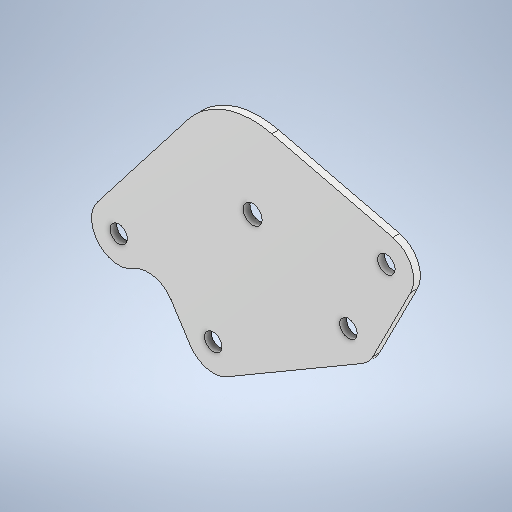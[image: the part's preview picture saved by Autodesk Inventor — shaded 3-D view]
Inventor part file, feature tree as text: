
AUTODESK INVENTOR PART (.ipt)
format: ipt  version: 2025.2 (Build 292293000, 293)  size: 270,336 bytes
history: native  units: in
note: dims shown in document units (in); Inventor stores cm internally (conversion verified against a paired STEP export)
features: other x5, sketch x2, plane x1, sheet_metal_op x1, extrude x1, reference x1
ambient origin geometry x8: Origin, YZ Plane, XZ Plane, XY Plane, X Axis, Y Axis, Z Axis, Center Point
bodies: Body1 (feature_tree)
feature tree (11):
  plane  "Work Plane1"
  sheet_metal_op  "Face3"
  extrude  "Extrusion1"  Depth=0.16in
  sketch  "Sketch1"  dims[d1=0.5in d14=0.16in]
  reference  "Reference3"
  other  "Plate3"
  sketch  "Sketch2"  dims[d15=0.0625in d16=0.175in d17=0.175in d18=0.625in d19=0.0in]
  parser-record x1  (decoder bookkeeping rows leaked as tree rows — omitted from the tree; the rows remain in map.json)
  other  "ACE 2.0.iam"
  other  "V5 Rotation Sensor:4"
  other  "Rear Vertical Odom Pod Rot Side:2"
note: 1 file-system path scrubbed to <path> (originals preserved in map.json)
